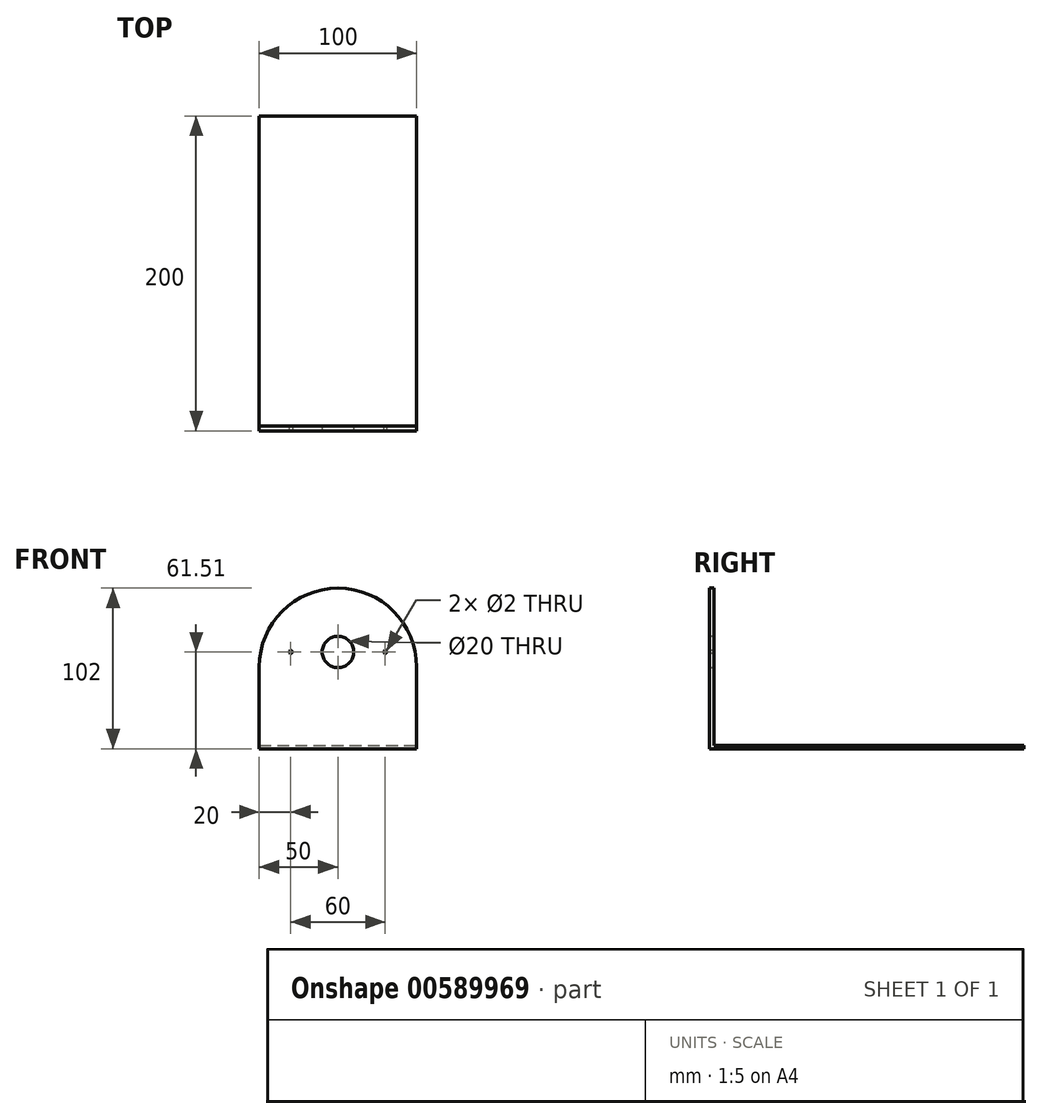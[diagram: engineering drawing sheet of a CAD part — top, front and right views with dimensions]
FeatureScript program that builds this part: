
annotation { "Feature Type Name" : "Feature", "Feature Type Description" : "" }
export const myFeature = defineFeature(function(context is Context, id is Id, definition is map)
    precondition{}
    {
        {
            var Q0;
            Q0=qCreatedBy(makeId("Top.planeOp"),FACE);
            var sketch = newSketch(context, id + "F0", { "sketchPlane" : qUnion([Q0])});
            skLineSegment(sketch, "E0.bottom", {"start": v(50, 100) * mm, "end": v(-50, 100) * mm});
            skLineSegment(sketch, "E0.top", {"start": v(50, -100) * mm, "end": v(-50, -100) * mm});
            skLineSegment(sketch, "E0.left", {"start": v(50, 100) * mm, "end": v(50, -100) * mm});
            skLineSegment(sketch, "E0.right", {"start": v(-50, 100) * mm, "end": v(-50, -100) * mm});
            skPoint(sketch, "E0.middle", {"position": v(0, 0) * mm});
            skSolve(sketch);
        }
        {
            var Q0;
            Q0=makeQuery(id+"F0.imprint","IMPRINT",FACE,{"disambiguationData":[TD([[makeQuery(id+"F0.imprint","IMPRINT",EDGE,{"derivedFrom":sQuery(id+"F0.wireOp",EDGE,"E0.bottom")}),1.0]])]});
            extrude(context, id + "F1", {"entities" : qUnion([Q0]), "depth" : 2 * mm, "offsetDistance" : 25 * mm});
        }
        {
            var Q0;
            Q0=makeQuery(id+"F1.opExtrude","CAP_FACE",FACE,{"disambiguationData":[OSD([sQuery(id+"F0.wireOp",EDGE,"E0.bottom"),sQuery(id+"F0.wireOp",EDGE,"E0.top"),sQuery(id+"F0.wireOp",EDGE,"E0.left"),sQuery(id+"F0.wireOp",EDGE,"E0.right")])],"isStart":false});
            var sketch = newSketch(context, id + "F2", { "sketchPlane" : qUnion([Q0])});
            skLineSegment(sketch, "E1.bottom", {"start": v(-50, -100) * mm, "end": v(50, -100) * mm});
            skLineSegment(sketch, "E1.top", {"start": v(-50, -97) * mm, "end": v(50, -97) * mm});
            skLineSegment(sketch, "E1.left", {"start": v(-50, -100) * mm, "end": v(-50, -97) * mm});
            skLineSegment(sketch, "E1.right", {"start": v(50, -100) * mm, "end": v(50, -97) * mm});
            skSolve(sketch);
        }
        {
            var Q0;
            Q0=makeQuery(id+"F2.imprint","IMPRINT",FACE,{"disambiguationData":[TD([[makeQuery(id+"F2.imprint","IMPRINT",EDGE,{"derivedFrom":sQuery(id+"F2.wireOp",EDGE,"E1.bottom")}),-1.0]])]});
            extrude(context, id + "F3", {"entities" : qUnion([Q0]), "operationType" : NewBodyOperationType.ADD, "depth" : 100 * mm, "offsetDistance" : 25 * mm});
        }
        {
            var Q0;
            Q0=makeQuery(id+"F3.opExtrude","CAP_EDGE",EDGE,{"disambiguationData":[OSD([sQuery(id+"F2.wireOp",EDGE,"E1.left")])],"isStart":false});
            var Q1;
            Q1=makeQuery(id+"F3.opExtrude","CAP_EDGE",EDGE,{"disambiguationData":[OSD([sQuery(id+"F2.wireOp",EDGE,"E1.right")])],"isStart":false});
            fillet(context, id + "F4", {"entities" : qUnion([Q0, Q1]), "radius" : 50 * mm, "tangentPropagation" : true, "allowEdgeOverflow" : false});
        }
        {
            var Q0;
            Q0=makeQuery(id+"F3.boolean.opBoolean","MERGE",FACE,{"derivedFrom":[makeQuery(id+"F1.opExtrude","SWEPT_FACE",FACE,{"disambiguationData":[OSD([sQuery(id+"F0.wireOp",EDGE,"E0.top")])]}),makeQuery(id+"F3.opExtrude","SWEPT_FACE",FACE,{"disambiguationData":[OSD([sQuery(id+"F2.wireOp",EDGE,"E1.bottom")])]})]});
            var sketch = newSketch(context, id + "F5", { "sketchPlane" : qUnion([Q0])});
            skCircle(sketch, "E2", {"center": v(0, 61.5) * mm, "radius": 10 * mm});
            skCircle(sketch, "E3", {"center": v(30, 61.5) * mm, "radius": 1 * mm});
            skCircle(sketch, "E4", {"center": v(-30, 61.5) * mm, "radius": 1 * mm});
            skSolve(sketch);
        }
        {
            var Q0;
            Q0=makeQuery(id+"F5.imprint","IMPRINT",FACE,{"disambiguationData":[TD([[makeQuery(id+"F5.imprint","IMPRINT",EDGE,{"derivedFrom":sQuery(id+"F5.wireOp",EDGE,"E2")}),1.0]])]});
            extrude(context, id + "F6", {"entities" : qUnion([Q0]), "operationType" : NewBodyOperationType.REMOVE, "oppositeDirection" : true, "depth" : 25 * mm, "offsetDistance" : 25 * mm});
        }
        {
            var Q0;
            Q0 = qSketchRegion(id + "F5", true);
            extrude(context, id + "F7", {"entities" : qUnion([Q0]), "operationType" : NewBodyOperationType.REMOVE, "oppositeDirection" : true, "depth" : 25 * mm, "offsetDistance" : 25 * mm});
        }
    });
